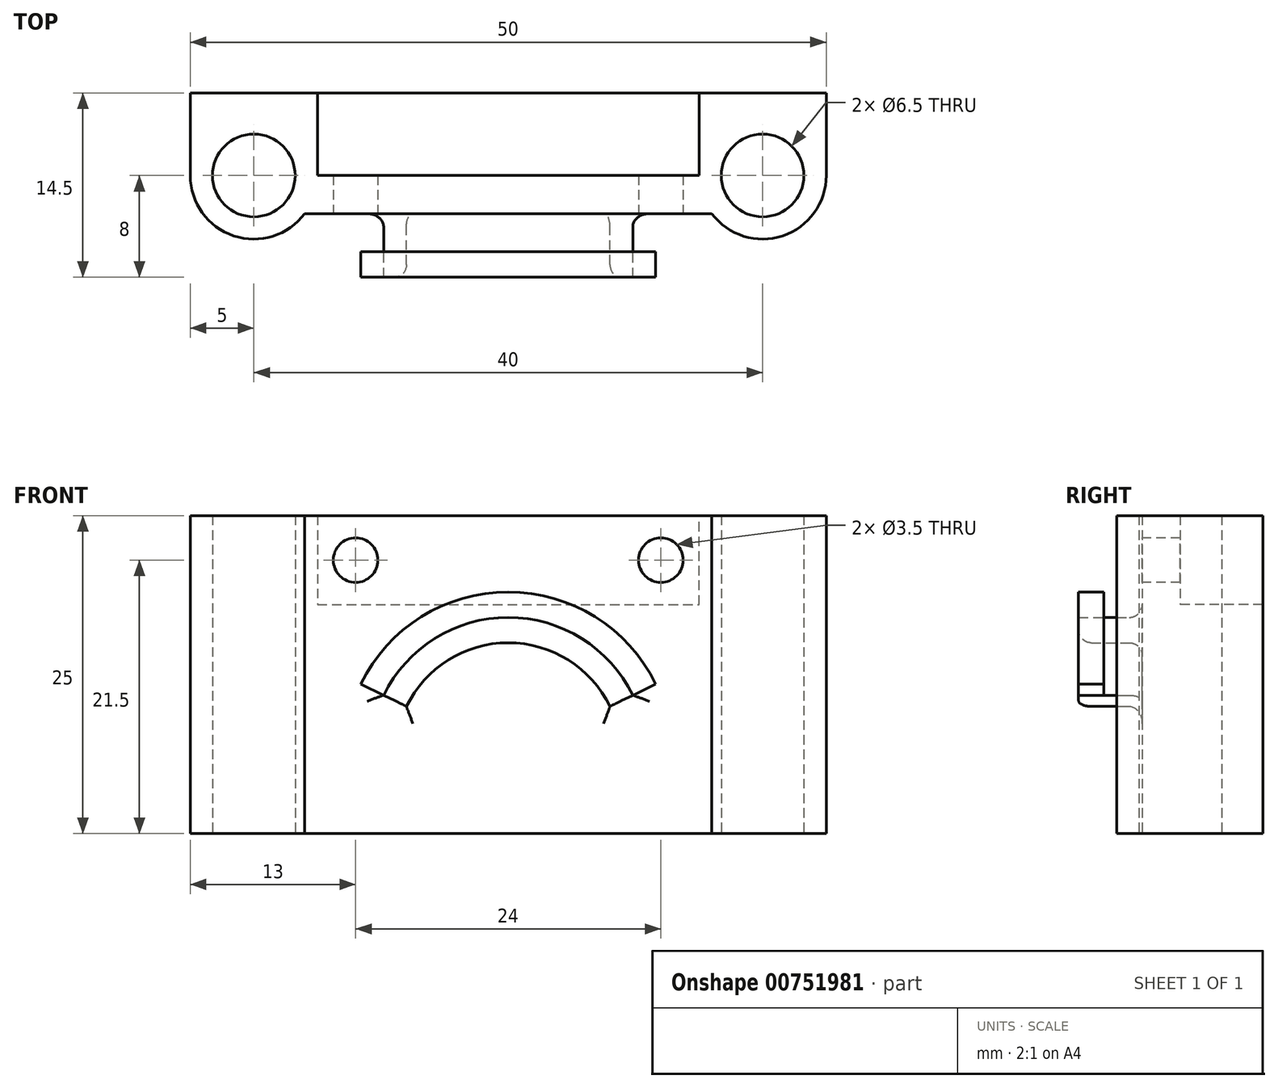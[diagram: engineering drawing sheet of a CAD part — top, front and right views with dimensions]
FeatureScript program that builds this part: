
annotation { "Feature Type Name" : "Feature", "Feature Type Description" : "" }
export const myFeature = defineFeature(function(context is Context, id is Id, definition is map)
    precondition{}
    {
        {
            var Q0;
            Q0=qCreatedBy(makeId("Top.planeOp"),FACE);
            var sketch = newSketch(context, id + "F0", { "sketchPlane" : qUnion([Q0])});
            skLineSegment(sketch, "E0", {"start": v(0, 0) * mm, "end": v(-20, 0) * mm, "construction": true});
            skCircle(sketch, "E1", {"center": v(-20, 0) * mm, "radius": 3.25 * mm});
            skArc(sketch, "E2", {"start": v(-25, 0) * mm, "mid": v(-21.58, -4.74) * mm, "end": v(-16, -3) * mm});
            skLineSegment(sketch, "E3", {"start": v(0, 0) * mm, "end": v(0, -3) * mm, "construction": true});
            skLineSegment(sketch, "E4", {"start": v(0, -3) * mm, "end": v(-16, -3) * mm});
            skLineSegment(sketch, "E5", {"start": v(-25, 0) * mm, "end": v(-25, 20) * mm});
            skLineSegment(sketch, "E6", {"start": v(-25, 20) * mm, "end": v(-25, 6.5) * mm});
            skLineSegment(sketch, "E7", {"start": v(-25, 20) * mm, "end": v(0, 20) * mm});
            skLineSegment(sketch, "E8.MirrorCS", {"start": v(25, 20) * mm, "end": v(0, 20) * mm});
            skLineSegment(sketch, "E9.MirrorCS", {"start": v(25, 20) * mm, "end": v(25, 6.5) * mm});
            skLineSegment(sketch, "E10.MirrorCS", {"start": v(25, 0) * mm, "end": v(25, 20) * mm});
            skArc(sketch, "E11.MirrorCS", {"start": v(25, 0) * mm, "mid": v(21.58, -4.74) * mm, "end": v(16, -3) * mm});
            skLineSegment(sketch, "E12.MirrorCS", {"start": v(0, -3) * mm, "end": v(16, -3) * mm});
            skCircle(sketch, "E13.MirrorC", {"center": v(20, 0) * mm, "radius": 3.25 * mm});
            skLineSegment(sketch, "E14", {"start": v(-25, 6.5) * mm, "end": v(25, 6.5) * mm});
            skSolve(sketch);
        }
        {
            var Q0;
            Q0=makeQuery(id+"F0.imprint","IMPRINT",FACE,{"disambiguationData":[TD([[makeQuery(id+"F0.imprint","IMPRINT",EDGE,{"derivedFrom":sQuery(id+"F0.wireOp",EDGE,"E1")}),-1.0]])]});
            extrude(context, id + "F1", {"entities" : qUnion([Q0]), "depth" : 25 * mm, "offsetDistance" : 25 * mm});
        }
        {
            var Q0;
            Q0=qCreatedBy(makeId("Front.planeOp"),FACE);
            var sketch = newSketch(context, id + "F2", { "sketchPlane" : qUnion([Q0])});
            skLineSegment(sketch, "E15", {"start": v(0, 0) * mm, "end": v(0, 15) * mm, "construction": true});
            skLineSegment(sketch, "E16", {"start": v(0, 15) * mm, "end": v(8, 15) * mm, "construction": true});
            skLineSegment(sketch, "E17", {"start": v(8, 15) * mm, "end": v(8, 10) * mm, "construction": true});
            skLineSegment(sketch, "E18.MirrorCS", {"start": v(0, 15) * mm, "end": v(-8, 15) * mm, "construction": true});
            skLineSegment(sketch, "E19.MirrorCS", {"start": v(-8, 15) * mm, "end": v(-8, 10) * mm, "construction": true});
            skArc(sketch, "E20", {"start": v(8, 10) * mm, "mid": v(0, 15) * mm, "end": v(-8, 10) * mm});
            skArc(sketch, "E21.0", {"start": v(9.8, 10.88) * mm, "mid": v(0, 17) * mm, "end": v(-9.8, 10.88) * mm});
            skArc(sketch, "E22.0", {"start": v(11.6, 11.75) * mm, "mid": v(0, 19) * mm, "end": v(-11.6, 11.75) * mm});
            skLineSegment(sketch, "E23", {"start": v(-8, 10) * mm, "end": v(-11.6, 11.75) * mm});
            skLineSegment(sketch, "E24", {"start": v(8, 10) * mm, "end": v(11.6, 11.75) * mm});
            skSolve(sketch);
        }
        {
            var Q0;
            {var subQ0=sQuery(id+"F2.wireOp",EDGE,"E20");Q0=makeQuery(id+"F2.imprint","IMPRINT",FACE,{"disambiguationData":[TD([[makeQuery(id+"F2.imprint","IMPRINT",EDGE,{"derivedFrom":subQ0}),-1.0]])]});}
            extrude(context, id + "F3", {"entities" : qUnion([Q0]), "operationType" : NewBodyOperationType.ADD, "depth" : 8 * mm, "offsetDistance" : 25 * mm});
        }
        {
            var Q0;
            {var subQ0=sQuery(id+"F2.wireOp",EDGE,"E21.0");Q0=makeQuery(id+"F2.imprint","IMPRINT",FACE,{"disambiguationData":[TD([[makeQuery(id+"F2.imprint","IMPRINT",EDGE,{"derivedFrom":subQ0}),-1.0]])]});}
            extrude(context, id + "F4", {"entities" : qUnion([Q0]), "depth" : 8 * mm, "offsetDistance" : 25 * mm, "hasSecondDirection" : true, "secondDirectionOppositeDirection" : false, "secondDirectionDepth" : 6 * mm});
        }
        {
            var Q0;
            Q0=qCreatedBy(makeId("Front.planeOp"),FACE);
            var sketch = newSketch(context, id + "F5", { "sketchPlane" : qUnion([Q0])});
            skLineSegment(sketch, "E25", {"start": v(0, 0) * mm, "end": v(0, 18) * mm, "construction": true});
            skLineSegment(sketch, "E26", {"start": v(0, 18) * mm, "end": v(-15, 18) * mm});
            skLineSegment(sketch, "E27", {"start": v(-15, 18) * mm, "end": v(-15, 26) * mm});
            skLineSegment(sketch, "E28", {"start": v(-15, 26) * mm, "end": v(15, 26) * mm});
            skLineSegment(sketch, "E29", {"start": v(15, 26) * mm, "end": v(15, 18) * mm});
            skLineSegment(sketch, "E30", {"start": v(15, 18) * mm, "end": v(0, 18) * mm});
            skSolve(sketch);
        }
        {
            var Q0;
            Q0=makeQuery(id+"F5.imprint","IMPRINT",FACE,{"disambiguationData":[TD([[makeQuery(id+"F5.imprint","IMPRINT",EDGE,{"derivedFrom":sQuery(id+"F5.wireOp",EDGE,"E26")}),-1.0]])]});
            extrude(context, id + "F6", {"entities" : qUnion([Q0]), "operationType" : NewBodyOperationType.REMOVE, "oppositeDirection" : true, "depth" : 25 * mm, "offsetDistance" : 25 * mm});
        }
        {
            var Q0;
            Q0=qCreatedBy(makeId("Front.planeOp"),FACE);
            var sketch = newSketch(context, id + "F7", { "sketchPlane" : qUnion([Q0])});
            skLineSegment(sketch, "E31", {"start": v(0, 0) * mm, "end": v(0, 21.5) * mm, "construction": true});
            skLineSegment(sketch, "E32", {"start": v(0, 21.5) * mm, "end": v(-12, 21.5) * mm, "construction": true});
            skCircle(sketch, "E33", {"center": v(-12, 21.5) * mm, "radius": 1.75 * mm});
            skCircle(sketch, "E34.MirrorC", {"center": v(12, 21.5) * mm, "radius": 1.75 * mm});
            skSolve(sketch);
        }
        {
            var Q0;
            Q0 = qSketchRegion(id + "F7", true);
            extrude(context, id + "F8", {"entities" : qUnion([Q0]), "operationType" : NewBodyOperationType.REMOVE, "oppositeDirection" : true, "depth" : 25 * mm, "offsetDistance" : 25 * mm, "hasSecondDirection" : true, "secondDirectionOppositeDirection" : false, "secondDirectionDepth" : 25 * mm});
        }
        {
            var Q0;
            Q0=makeQuery(id+"F3.boolean.opBoolean","INTERSECT",EDGE,{"derivedFrom":[makeQuery(id+"F1.opExtrude","SWEPT_FACE",FACE,{"disambiguationData":[OSD([sQuery(id+"F0.wireOp",EDGE,"E4"),sQuery(id+"F0.wireOp",EDGE,"E12.MirrorCS")])]}),makeQuery(id+"F3.opExtrude","SWEPT_FACE",FACE,{"disambiguationData":[OSD([sQuery(id+"F2.wireOp",EDGE,"E20")])]})]});
            var Q1;
            Q1=makeQuery(id+"F3.boolean.opBoolean","INTERSECT",EDGE,{"derivedFrom":[makeQuery(id+"F1.opExtrude","SWEPT_FACE",FACE,{"disambiguationData":[OSD([sQuery(id+"F0.wireOp",EDGE,"E4"),sQuery(id+"F0.wireOp",EDGE,"E12.MirrorCS")])]}),makeQuery(id+"F3.opExtrude","SWEPT_FACE",FACE,{"disambiguationData":[OSD([sQuery(id+"F2.wireOp",EDGE,"E23")])]})]});
            var Q2;
            Q2=makeQuery(id+"F3.boolean.opBoolean","INTERSECT",EDGE,{"derivedFrom":[makeQuery(id+"F1.opExtrude","SWEPT_FACE",FACE,{"disambiguationData":[OSD([sQuery(id+"F0.wireOp",EDGE,"E4"),sQuery(id+"F0.wireOp",EDGE,"E12.MirrorCS")])]}),makeQuery(id+"F3.opExtrude","SWEPT_FACE",FACE,{"disambiguationData":[OSD([sQuery(id+"F2.wireOp",EDGE,"E24")])]})]});
            var Q3;
            Q3=makeQuery(id+"F3.boolean.opBoolean","INTERSECT",EDGE,{"derivedFrom":[makeQuery(id+"F1.opExtrude","SWEPT_FACE",FACE,{"disambiguationData":[OSD([sQuery(id+"F0.wireOp",EDGE,"E4"),sQuery(id+"F0.wireOp",EDGE,"E12.MirrorCS")])]}),makeQuery(id+"F3.opExtrude","SWEPT_FACE",FACE,{"disambiguationData":[OSD([sQuery(id+"F2.wireOp",EDGE,"E21.0")])]})]});
            var Q4;
            Q4=makeQuery(id+"F3.opExtrude","CAP_EDGE",EDGE,{"disambiguationData":[OSD([sQuery(id+"F2.wireOp",EDGE,"E20")])],"isStart":false});
            fillet(context, id + "F9", {"entities" : qUnion([Q0, Q1, Q2, Q3, Q4]), "radius" : 1 * mm, "tangentPropagation" : true, "allowEdgeOverflow" : false});
        }
    });
